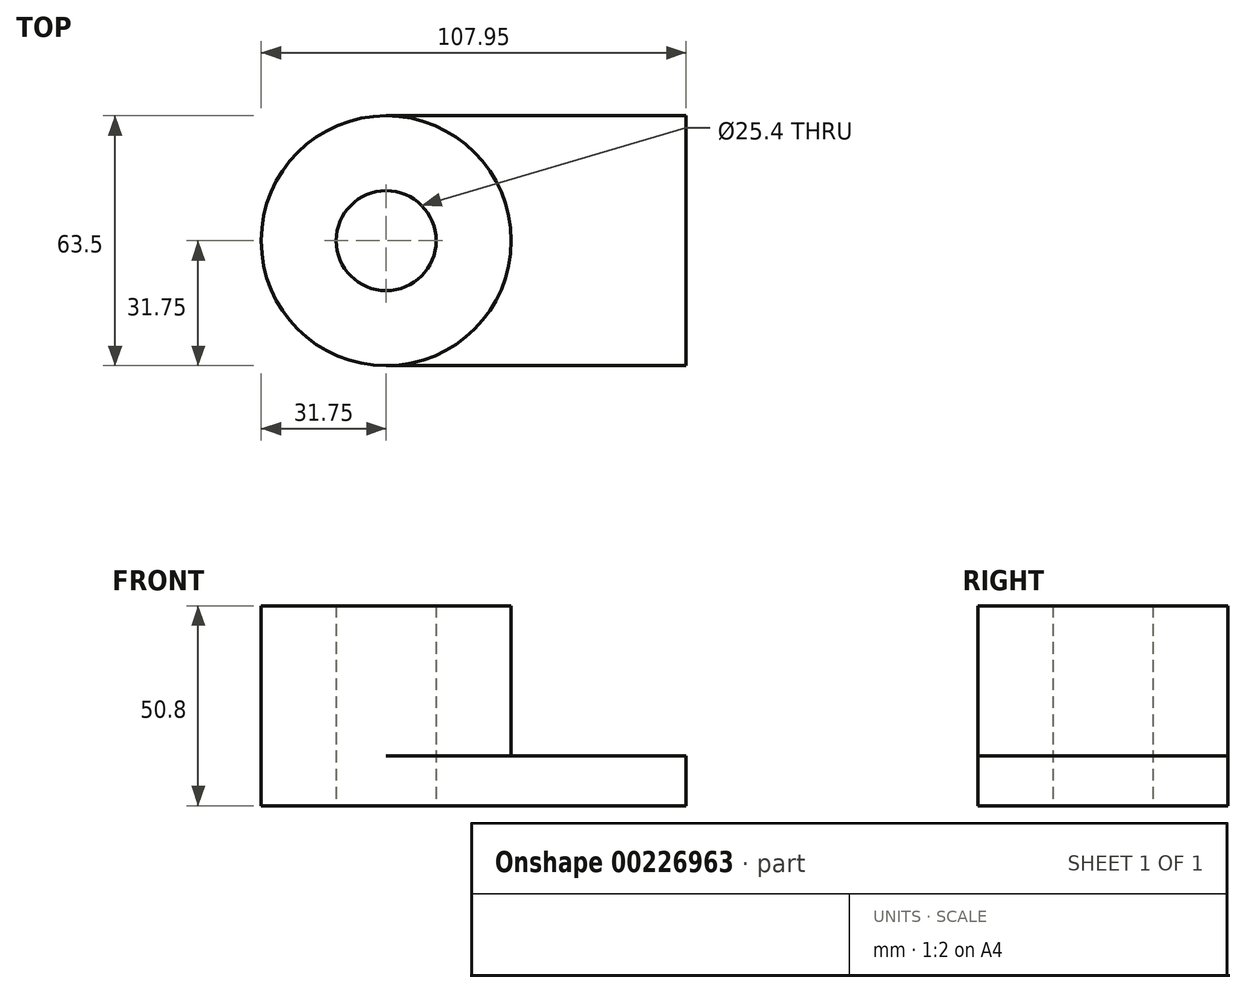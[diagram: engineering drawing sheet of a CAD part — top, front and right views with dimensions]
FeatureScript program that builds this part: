
annotation { "Feature Type Name" : "Feature", "Feature Type Description" : "" }
export const myFeature = defineFeature(function(context is Context, id is Id, definition is map)
    precondition{}
    {
        {
            var Q0;
            Q0=qCreatedBy(makeId("Top.planeOp"),FACE);
            var sketch = newSketch(context, id + "F0", { "sketchPlane" : qUnion([Q0])});
            skLineSegment(sketch, "E0.bottom", {"start": v(-38.1, 31.75) * mm, "end": v(38.1, 31.75) * mm});
            skLineSegment(sketch, "E0.top", {"start": v(-38.1, -31.75) * mm, "end": v(38.1, -31.75) * mm});
            skLineSegment(sketch, "E0.left", {"start": v(-38.1, 31.75) * mm, "end": v(-38.1, -31.75) * mm});
            skLineSegment(sketch, "E0.right", {"start": v(38.1, 31.75) * mm, "end": v(38.1, -31.75) * mm});
            skPoint(sketch, "E0.middle", {"position": v(0, 0) * mm});
            skCircle(sketch, "E1", {"center": v(-38.1, 0) * mm, "radius": 31.75 * mm});
            skCircle(sketch, "E2", {"center": v(-38.1, 0) * mm, "radius": 12.7 * mm});
            skSolve(sketch);
        }
        {
            var Q0;
            Q0 = qSketchRegion(id + "F0", true);
            extrude(context, id + "F1", {"entities" : qUnion([Q0]), "depth" : 12.7 * mm});
        }
        {
            var Q0;
            {var subQ1=sQuery(id+"F0.wireOp",EDGE,"E0.left");var subQ3=sQuery(id+"F0.wireOp",EDGE,"E2");var subQ4=makeQuery(id+"F0.imprint","INTERSECT",VERTEX,{"disambiguationData":[OD(0.0)],"derivedFrom":[subQ1,subQ3]});Q0=makeQuery(id+"F0.imprint","IMPRINT",FACE,{"disambiguationData":[TD([[makeQuery(id+"F0.imprint","IMPRINT",EDGE,{"disambiguationData":[TD([[subQ4,-1.0]])],"derivedFrom":subQ3}),-1.0]])]});}
            extrude(context, id + "F2", {"entities" : qUnion([Q0]), "operationType" : NewBodyOperationType.ADD, "depth" : 50.8 * mm});
        }
        {
            var Q0;
            {var subQ1=sQuery(id+"F0.wireOp",EDGE,"E0.left");var subQ3=sQuery(id+"F0.wireOp",EDGE,"E2");var subQ4=makeQuery(id+"F0.imprint","INTERSECT",VERTEX,{"disambiguationData":[OD(0.0)],"derivedFrom":[subQ1,subQ3]});Q0=makeQuery(id+"F0.imprint","IMPRINT",FACE,{"disambiguationData":[TD([[makeQuery(id+"F0.imprint","IMPRINT",EDGE,{"disambiguationData":[TD([[subQ4,1.0]])],"derivedFrom":subQ3}),-1.0]])]});}
            extrude(context, id + "F3", {"entities" : qUnion([Q0]), "operationType" : NewBodyOperationType.ADD, "depth" : 50.8 * mm});
        }
    });
